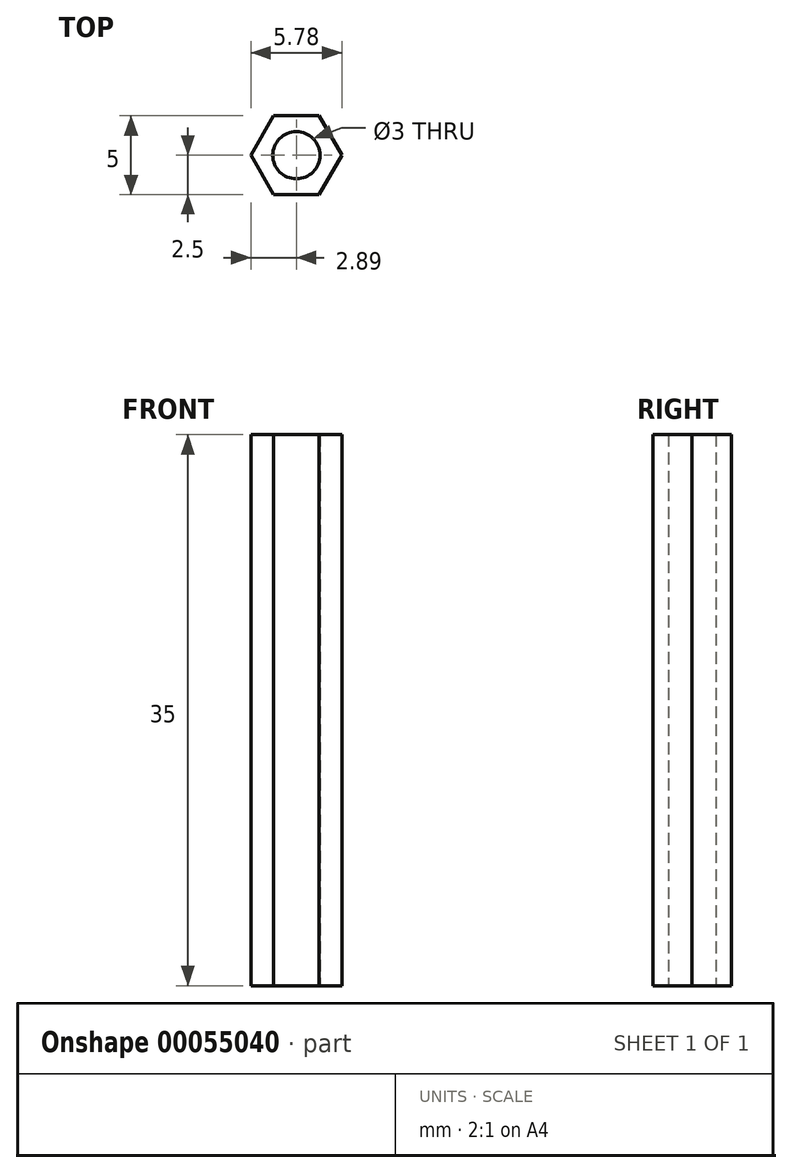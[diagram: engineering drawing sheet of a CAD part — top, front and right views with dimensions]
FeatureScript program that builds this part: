
annotation { "Feature Type Name" : "Feature", "Feature Type Description" : "" }
export const myFeature = defineFeature(function(context is Context, id is Id, definition is map)
    precondition{}
    {
        {
            var Q0;
            Q0=qCreatedBy(makeId("Top.planeOp"),FACE);
            var sketch = newSketch(context, id + "F0", { "sketchPlane" : qUnion([Q0])});
            skCircle(sketch, "E0.cCircle", {"center": v(0, 0) * mm, "radius": 2.5 * mm, "construction": true});
            skLineSegment(sketch, "E0.0", {"start": v(1.44, -2.5) * mm, "end": v(-1.44, -2.5) * mm});
            skLineSegment(sketch, "E0.1", {"start": v(-1.44, -2.5) * mm, "end": v(-2.89, 0) * mm});
            skLineSegment(sketch, "E0.2", {"start": v(-2.89, 0) * mm, "end": v(-1.44, 2.5) * mm});
            skLineSegment(sketch, "E0.3", {"start": v(-1.44, 2.5) * mm, "end": v(1.44, 2.5) * mm});
            skLineSegment(sketch, "E0.4", {"start": v(1.44, 2.5) * mm, "end": v(2.89, 0) * mm});
            skLineSegment(sketch, "E0.5", {"start": v(2.89, 0) * mm, "end": v(1.44, -2.5) * mm});
            skPoint(sketch, "E0.0.midPoint", {"position": v(0, -2.5) * mm});
            skCircle(sketch, "E1", {"center": v(0, 0) * mm, "radius": 1.5 * mm});
            skSolve(sketch);
        }
        {
            var Q0;
            Q0=qSketchRegion(id+"F0",true);
            extrude(context, id + "F1", {"entities" : qUnion([Q0]), "depth" : 35 * mm});
        }
    });
